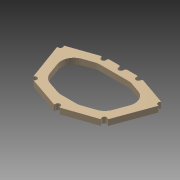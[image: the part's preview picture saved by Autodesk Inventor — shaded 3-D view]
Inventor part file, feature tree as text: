
AUTODESK INVENTOR PART (.ipt)
format: ipt  version: 2015 (Build 190159000, 159)  size: 193,536 bytes
history: native  units: mm
features: fillet x6, hole x5, extrude x2, sketch x2, mirror x1
ambient origin geometry x8: Origin, YZ Plane, XZ Plane, XY Plane, X Axis, Y Axis, Z Axis, Center Point
bodies: Solid4 (feature_tree)
feature tree (16):
  extrude  "Extrusion4"  Depth=228.6mm
  hole  "Hole2"  [1 undecoded]
  hole  "Hole3"  [1 undecoded]
  hole  "Hole4"  [1 undecoded]
  hole  "Hole5"  [1 undecoded]
  hole  "Hole6"  [1 undecoded]
  fillet  "Fillet6"  Radius=18.0mm
  fillet  "Fillet7"  Radius=5.5mm
  fillet  "Fillet8"  Radius=4.0mm
  fillet  "Fillet9"  Radius=1.0mm
  fillet  "Fillet10"  Radius=1.0mm
  extrude  "Extrusion5"  Depth=2.0mm
  fillet  "Fillet11"  Radius=28.0mm
  mirror  "Mirror3"
  sketch  "Sketch1"  dims[d9=228.6mm d11=161.8488mm]
  sketch  "Sketch4"  dims[d15=191.7192mm d20=112.776mm d22=57.6072mm d39=55.7784mm d41=0.0mm d42=19.2024mm d98=18.0mm d99=0.0mm d159=10.0mm d160=10.0mm d102=15.0mm d103=6.0mm d104=3.023mm d105=2.0mm d106=14.3117mm d107=8.0mm d108=20.594885mm d167=10.0mm d168=10.0mm d111=15.0mm d112=6.0mm d113=3.023mm d114=2.0mm d115=14.3117mm d116=8.0mm d117=20.594885mm d161=10.0mm d162=10.0mm d124=15.0mm d125=6.0mm d126=3.023mm d127=2.0mm d128=14.3117mm d129=8.0mm d130=20.594885mm d163=10.0mm d164=10.0mm d133=15.0mm d134=6.0mm d135=3.023mm d136=2.0mm d137=14.3117mm d138=8.0mm d139=20.594885mm d165=10.0mm d166=10.0mm d150=15.0mm d151=6.0mm d152=4.0mm d153=2.0mm d154=90.0deg d155=8.0mm d156=20.594885mm d157=5.5mm d158=4.0mm d169=1.0mm d170=1.0mm d171=2.0mm d172=28.0mm d173=28.0mm d174=28.0mm d175=28.0mm d176=30.0mm d177=10.0mm d178=0.0mm d179=40.0mm]
note: 5 required parameter values undecoded (feature->parameter linkage not recoverable at this tier; creation-order binding heuristic only, values carry confidence <= 0.55)
